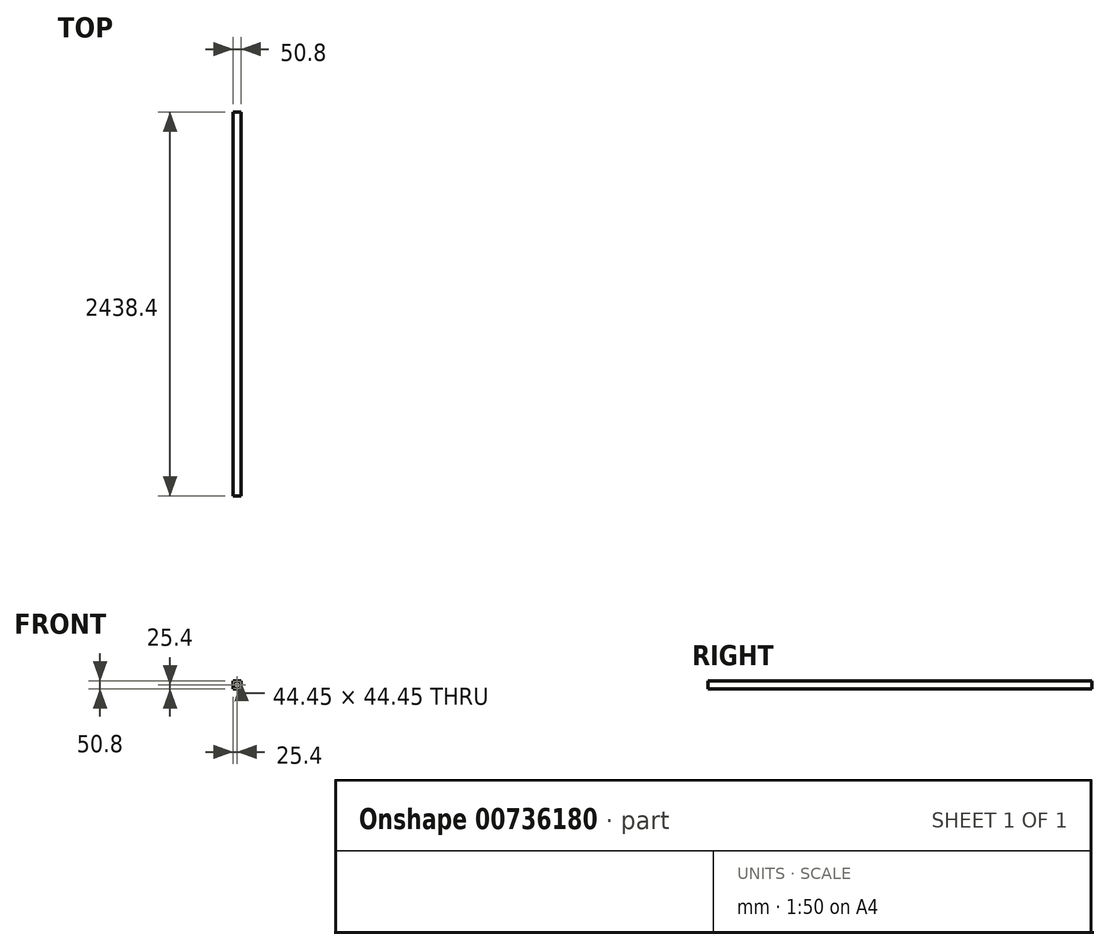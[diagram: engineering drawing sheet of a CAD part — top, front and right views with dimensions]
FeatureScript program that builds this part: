
annotation { "Feature Type Name" : "Feature", "Feature Type Description" : "" }
export const myFeature = defineFeature(function(context is Context, id is Id, definition is map)
    precondition{}
    {
        {
            var Q0;
            Q0=qCreatedBy(makeId("Front.planeOp"),FACE);
            var sketch = newSketch(context, id + "F0", { "sketchPlane" : qUnion([Q0])});
            skLineSegment(sketch, "E0.bottom", {"start": v(25.4, -25.4) * mm, "end": v(-25.4, -25.4) * mm});
            skLineSegment(sketch, "E0.top", {"start": v(25.4, 25.4) * mm, "end": v(-25.4, 25.4) * mm});
            skLineSegment(sketch, "E0.left", {"start": v(25.4, -25.4) * mm, "end": v(25.4, 25.4) * mm});
            skLineSegment(sketch, "E0.right", {"start": v(-25.4, -25.4) * mm, "end": v(-25.4, 25.4) * mm});
            skPoint(sketch, "E0.middle", {"position": v(0, 0) * mm});
            skLineSegment(sketch, "E1.bottom", {"start": v(22.23, -22.23) * mm, "end": v(-22.22, -22.23) * mm});
            skLineSegment(sketch, "E1.top", {"start": v(22.22, 22.23) * mm, "end": v(-22.23, 22.23) * mm});
            skLineSegment(sketch, "E1.left", {"start": v(22.23, -22.22) * mm, "end": v(22.23, 22.23) * mm});
            skLineSegment(sketch, "E1.right", {"start": v(-22.23, -22.23) * mm, "end": v(-22.23, 22.22) * mm});
            skSolve(sketch);
        }
        {
            var Q0;
            Q0 = qSketchRegion(id + "F0", true);
            extrude(context, id + "F1", {"entities" : qUnion([Q0]), "oppositeDirection" : true, "depth" : 2438.4 * mm, "offsetDistance" : 25.4 * mm});
        }
    });
